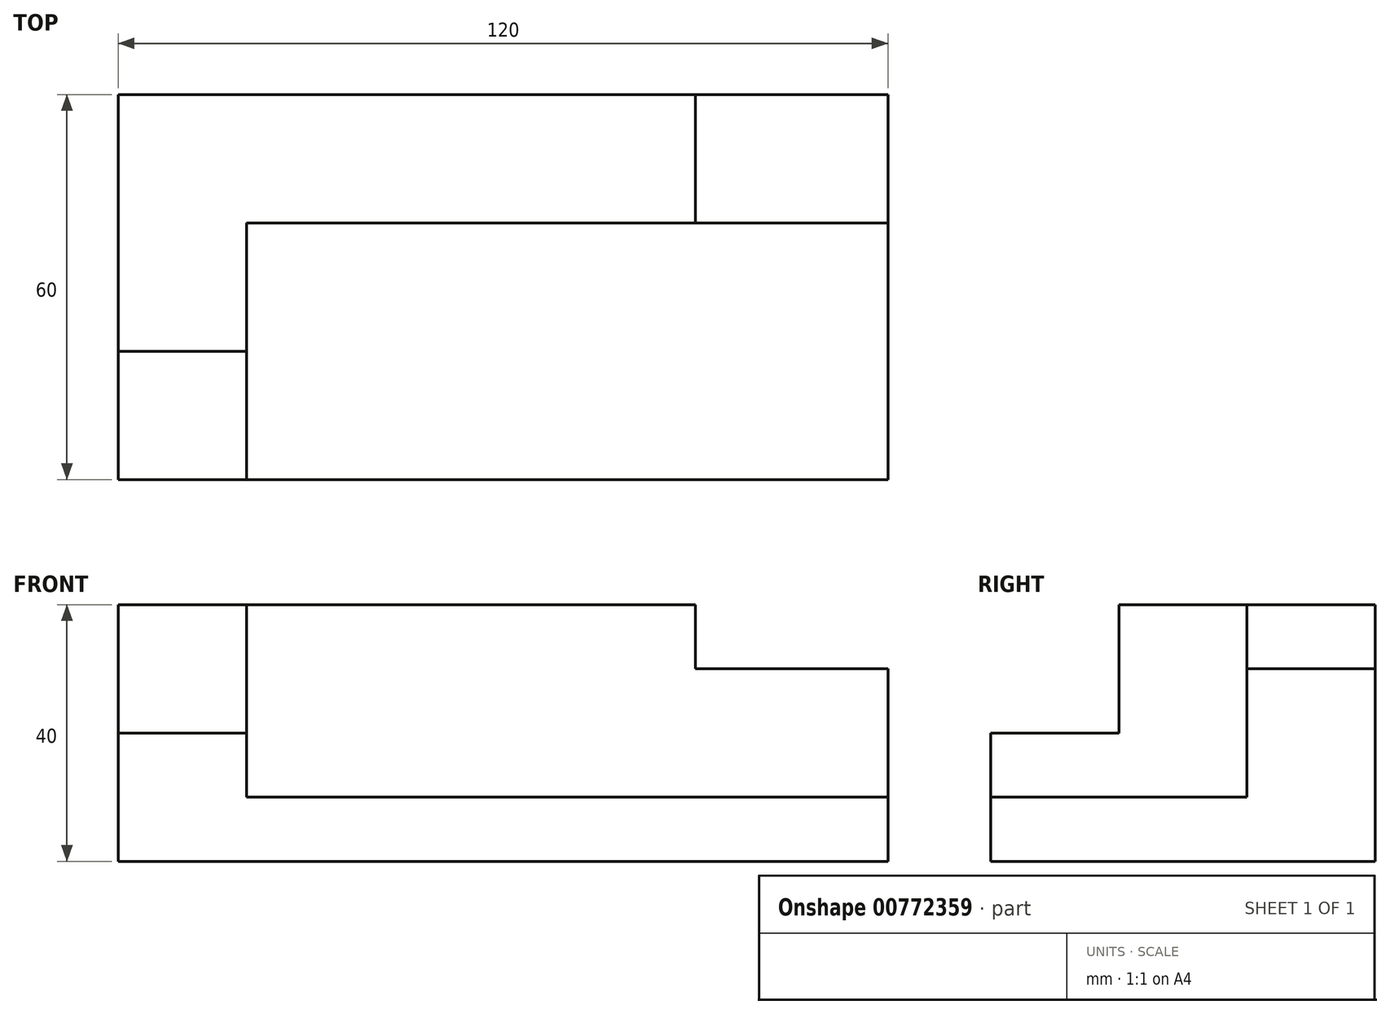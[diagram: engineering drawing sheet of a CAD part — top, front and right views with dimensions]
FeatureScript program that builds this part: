
annotation { "Feature Type Name" : "Feature", "Feature Type Description" : "" }
export const myFeature = defineFeature(function(context is Context, id is Id, definition is map)
    precondition{}
    {
        {
            var Q0;
            Q0=qCreatedBy(makeId("Top.planeOp"),FACE);
            var sketch = newSketch(context, id + "F0", { "sketchPlane" : qUnion([Q0])});
            skLineSegment(sketch, "E0.bottom", {"start": v(60, 30) * mm, "end": v(-60, 30) * mm});
            skLineSegment(sketch, "E0.top", {"start": v(60, -30) * mm, "end": v(-60, -30) * mm});
            skLineSegment(sketch, "E0.left", {"start": v(60, 30) * mm, "end": v(60, -30) * mm});
            skLineSegment(sketch, "E0.right", {"start": v(-60, 30) * mm, "end": v(-60, -30) * mm});
            skPoint(sketch, "E0.middle", {"position": v(0, 0) * mm});
            skLineSegment(sketch, "E1", {"start": v(-40, -30) * mm, "end": v(-40, 10) * mm});
            skLineSegment(sketch, "E2", {"start": v(-40, 10) * mm, "end": v(60, 10) * mm});
            skLineSegment(sketch, "E3", {"start": v(30, 30) * mm, "end": v(30, 10) * mm});
            skLineSegment(sketch, "E4", {"start": v(-40, -10) * mm, "end": v(-60, -10) * mm});
            skSolve(sketch);
        }
        {
            var Q0;
            Q0 = qSketchRegion(id + "F0", true);
            extrude(context, id + "F1", {"entities" : qUnion([Q0]), "oppositeDirection" : true, "depth" : 40 * mm, "offsetDistance" : 25 * mm});
        }
        {
            var Q0;
            {var subQ4=sQuery(id+"F0.wireOp",EDGE,"E0.top");var subQ6=sQuery(id+"F0.wireOp",EDGE,"E0.left");var subQ7=makeQuery(id+"F0.imprint","INTERSECT",VERTEX,{"derivedFrom":[subQ4,subQ6]});Q0=makeQuery(id+"F0.imprint","IMPRINT",FACE,{"disambiguationData":[TD([[makeQuery(id+"F0.imprint","IMPRINT",EDGE,{"disambiguationData":[TD([[subQ7,-1.0]])],"derivedFrom":subQ4}),-1.0]])]});}
            extrude(context, id + "F2", {"entities" : qUnion([Q0]), "operationType" : NewBodyOperationType.REMOVE, "oppositeDirection" : true, "depth" : 30 * mm, "offsetDistance" : 25 * mm});
        }
        {
            var Q0;
            {var subQ5=sQuery(id+"F0.wireOp",EDGE,"E4");Q0=makeQuery(id+"F0.imprint","IMPRINT",FACE,{"disambiguationData":[TD([[makeQuery(id+"F0.imprint","IMPRINT",EDGE,{"derivedFrom":subQ5}),1.0]])]});}
            extrude(context, id + "F3", {"entities" : qUnion([Q0]), "operationType" : NewBodyOperationType.REMOVE, "oppositeDirection" : true, "depth" : 20 * mm, "offsetDistance" : 25 * mm});
        }
        {
            var Q0;
            {var subQ3=sQuery(id+"F0.wireOp",EDGE,"E3");Q0=makeQuery(id+"F0.imprint","IMPRINT",FACE,{"disambiguationData":[TD([[makeQuery(id+"F0.imprint","IMPRINT",EDGE,{"derivedFrom":subQ3}),1.0]])]});}
            extrude(context, id + "F4", {"entities" : qUnion([Q0]), "operationType" : NewBodyOperationType.REMOVE, "oppositeDirection" : true, "depth" : 10 * mm, "offsetDistance" : 25 * mm});
        }
    });
